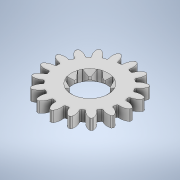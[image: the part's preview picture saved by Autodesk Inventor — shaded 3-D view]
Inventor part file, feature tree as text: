
AUTODESK INVENTOR PART (.ipt)
format: ipt  version: 2020 (Build 240168000, 168)  size: 780,288 bytes
history: native  units: mm
features: sketch x4, projected_geometry x4, extrude x3, chamfer x2, fillet x1, pattern_circular x1, mirror x1, revolve x1
ambient origin geometry x8: Origin, YZ Plane, XZ Plane, XY Plane, X Axis, Y Axis, Z Axis, Center Point
bodies: Solid1 (feature_tree)
feature tree (17):
  extrude  "Extrusion1"  Depth=170.0mm TaperAngle=360.0deg
  fillet  "Fillet2"  Radius=21.0mm
  pattern_circular  "Circular Pattern2"  [2 undecoded]
  extrude  "Extrusion4"  Depth=3.490659mm
  extrude  "Extrusion5"  Depth=0.308824mm
  mirror  "Mirror1"
  chamfer  "Chamfer1"  Distance=0.617647mm
  chamfer  "Chamfer2"  Distance=0.9702mm
  revolve  "Revolution1"  [1 undecoded]
  sketch  "Sketch1"  dims[d4=3.0mm d5=0.0mm d18=170.0mm d19=360.0deg d23=21.0mm]
  sketch  "Sketch3"  dims[d25=1.544118mm]
  sketch  "Sketch4"  dims[d26=1.235294mm]
  projected_geometry  "Projected Loop1"
  sketch  "Sketch6"  dims[d27=3.490659mm d28=19.733545mm d29=3.490659mm d30=0.308824mm d31=0.617647mm d32=0.9702mm d33=0.4mm d35=80.0mm d36=9.8mm d37=7.6mm d38=30.0deg d39=7.5mm d40=0.65mm d41=1.5708mm d42=0.32mm d43=360.0deg d58=8.0mm d59=10.2mm d60=8.9mm d61=1.5708mm d66=80.0mm d68=360.0deg d70=1.0mm d71=0.0mm d74=60.0deg d75=0.5mm d76=0.0mm d77=0.5mm d78=2.0mm d79=45.0deg d80=0.5mm d81=2.0mm d82=45.0deg d84=90.0deg d85=45.0deg d86=5.1mm]
  projected_geometry  "Projected Loop2"
  projected_geometry  "Projected Loop3"
  projected_geometry  "Projected Loop4"
note: 3 required parameter values undecoded (feature->parameter linkage not recoverable at this tier; creation-order binding heuristic only, values carry confidence <= 0.55)